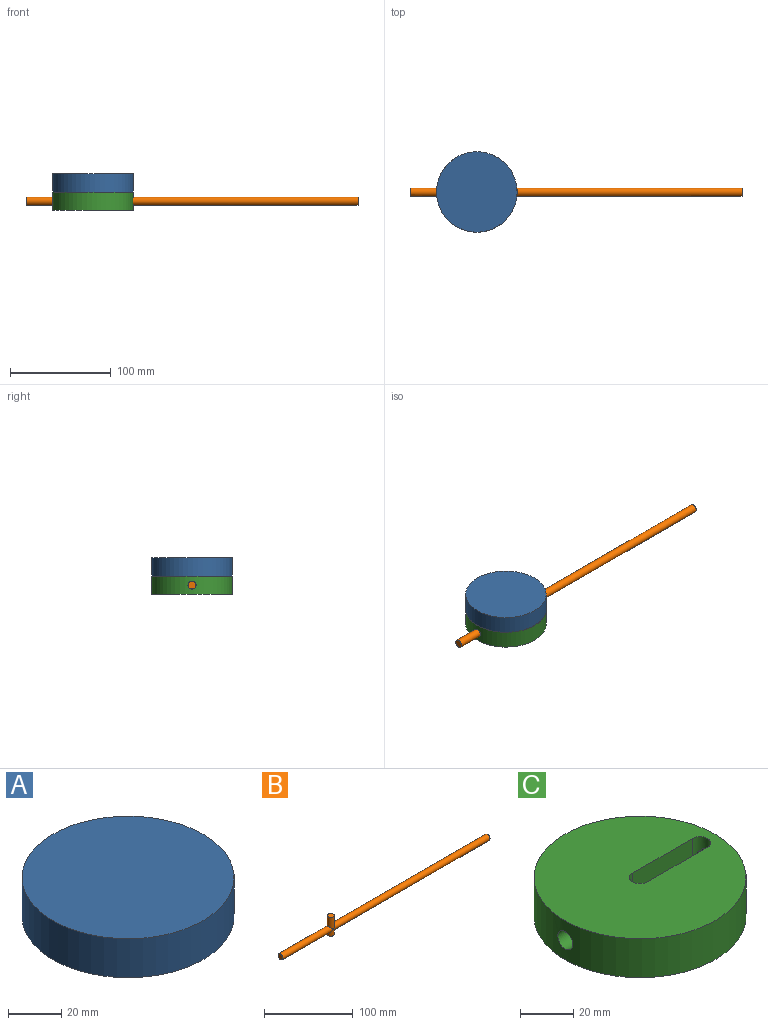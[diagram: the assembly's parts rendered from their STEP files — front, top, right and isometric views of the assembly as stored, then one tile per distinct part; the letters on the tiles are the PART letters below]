
ASSEMBLY  parts=3 mates=2
PART A: 12 faces, bbox 80x80x18 mm
  f0: plane 80x80mm, normal (0,0,-1), area 3669.4mm2, adj f1,f2,f3,f4,f5,f6,f7,f8
  f1: cylinder r=14mm len=28mm, axis (0,0,1), area 351.9mm2, adj f0,f2,f9,f10
  f2: cylinder r=4mm len=8mm, axis (0,0,1), area 100.5mm2, adj f0,f1,f3,f10
  f3: cylinder r=4mm len=8mm, axis (0,0,1), area 100.5mm2, adj f0,f2,f4,f10
  f4: cylinder r=12mm len=24mm, axis (0,0,1), area 301.6mm2, adj f0,f3,f5,f10
  f5: cylinder r=22mm len=44mm, axis (0,0,1), area 552.9mm2, adj f0,f4,f6,f10
  f6: cylinder r=30mm len=60mm, axis (0,0,1), area 754mm2, adj f0,f5,f7,f10
  f7: cylinder r=4mm len=8mm, axis (0,0,1), area 100.5mm2, adj f0,f6,f9,f10
  f8: cylinder r=40mm len=80mm, axis (0,0,1), area 4523.9mm2, adj f0,f11
  f9: cylinder r=22mm len=44mm, axis (0,0,1), area 552.9mm2, adj f0,f1,f7,f10
  f10: plane 60x52mm, normal (0,0,-1), area 1357.2mm2, adj f1,f2,f3,f4,f5,f6,f7,f9
  f11: plane 80x80mm, normal (0,0,1), area 5026.5mm2, adj f8
PART B: 8 faces, bbox 330x8x26 mm
  f0: cylinder r=4mm len=80mm, axis (-1,0,0), area 1946.6mm2, adj f1,f3,f4
  f1: plane 8x8mm, normal (-1,0,0), area 50.3mm2, adj f0
  f2: plane 8x8mm, normal (0,0,-1), area 50.3mm2, adj f3
  f3: cylinder r=4mm len=9mm, axis (0,0,1), area 162.2mm2, adj f0,f2,f7
  f4: cylinder r=4mm len=17mm, axis (0,0,1), area 363.3mm2, adj f0,f5,f7
  f5: plane 8x8mm, normal (0,0,1), area 50.3mm2, adj f4
  f6: plane 8x8mm, normal (1,0,0), area 50.3mm2, adj f7
  f7: cylinder r=4mm len=250mm, axis (-1,0,0), area 6219.2mm2, adj f3,f4,f6
PART C: 11 faces, bbox 80x80x18 mm
  f0: cylinder r=4mm len=9mm, axis (0,0,-1), area 81.1mm2, adj f5,f6,f8,f9
  f1: cylinder r=4mm len=9mm, axis (0,0,-1), area 81.1mm2, adj f5,f6,f7,f9
  f2: cylinder r=4mm len=9mm, axis (0,0,-1), area 81.1mm2, adj f5,f6,f7,f10
  f3: cylinder r=4mm len=9mm, axis (0,0,-1), area 81.1mm2, adj f5,f6,f8,f10
  f4: cylinder r=40mm len=80mm, axis (0,0,-1), area 4423.1mm2, adj f7,f8,f9,f10
  f5: plane 32x18mm, normal (0,1,0), area 576mm2, adj f0,f1,f2,f3,f7,f8
  f6: plane 32x18mm, normal (0,-1,0), area 576mm2, adj f0,f1,f2,f3,f7,f8
  f7: plane 80x80mm, normal (0,0,1), area 4720.3mm2, adj f1,f2,f4,f5,f6
  f8: plane 80x80mm, normal (0,0,-1), area 4720.3mm2, adj f0,f3,f4,f5,f6
  f9: cylinder r=4mm len=8mm, axis (-1,0,0), area 134.5mm2, adj f0,f1,f4
  f10: cylinder r=4mm len=40mm, axis (-1,0,0), area 938.8mm2, adj f2,f3,f4
PLACE A rot(axis=(0,0,-1),72.5deg) t=(0,0,0)mm
PLACE B t=(13.56,0,0)mm
PLACE C at identity fixed
MATE revolute A.f8 <-> C.f4  axis (0,0,-1) through (0,0,9)mm
MATE slider B.f0 <-> C.f9  axis (-1,0,0) through (-66.44,0,0)mm
